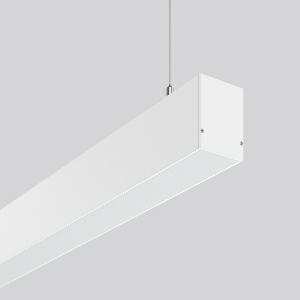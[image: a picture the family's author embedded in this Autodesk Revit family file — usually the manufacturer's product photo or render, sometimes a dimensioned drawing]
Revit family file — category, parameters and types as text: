
# Revit family: less_is_more_50_312320_002_76_c6af
name_source: partatom
category: Lighting Fixtures
units: mm (PartAtom-declared; Revit-internal decimal feet)

## family parameters
Cut with Voids When Loaded = No
Host = Face
Light Source = No
Part Type = Normal
Room Calculation Point = No
Round Connector Dimension = Use Diameter
Shared = No

## types (1)
- LESS IS MORE 50 (1 x LED Modul 830, 6900 lm, 3000)
    Apparent Load = 59 VA
    CIE Flux Codes = 49 80 96 63 100
    Color Rendering = 80
    Color Temperature = 3000
    Default Elevation = 1800 mm
    Description = Series: LESS IS MORE 50
Linear pendant luminaire for aesthetically sophisticated lighting. Housing: extruded aluminium profile, powder-coated. End cap aluminium powder-coated. Canopy made of aluminium, powder-coated. Diffuser made of non-yellowing plastic (PMMA), opal. Direct 65%, indirect 35% light emission. Suitable for pendant. 2-point steel cable suspension freely positionable and infinitely height-adjustable. Special lengths available on request. LED unit with integrated converter interchangeable and removable. Suitable for through-wiring. With sensors or as a safety luminaire on request. 
Colour: traffic white, matt (RAL 9016)
Length: 1687 mm
Width: 57 mm
Height: 75 mm
Suspension length: 2000 mm
Lamp: LED
Socket: without socket
Colour temperature: 3000K
Colour rendering index (CRI): 80
Light source: LED
Socket lamp2: Without base
Colour temperature: 3000K
System power: 59 W
Rated luminous flux: 6900 lm
Luminous efficiency: 117 lm/W
Control gear: Converter, dimmable, DALI
Control gear: Converter, dimmable, DALI
Protection class: I
Type of protection: IP 20
    Height = 75 mm
    Lamp = 1 x LED Modul 830
    Lamp Light Flux = 6900 lm
    Lamp count = 1
    Length = 1687 mm
    Lifetime = 50000 h
    Luminous efficacy = 117 lm/W
    Manufacturer = RZB
    ModVariant = No
    Model = 312320.002.76
    Mounting Place = Ceiling
    Mounting Type = Pendant
    Number of Poles = 1
    OnlyDefault = Yes
    Power Factor = 1
    Product Name = LESS IS MORE 50
    Product group = Pendant LED linear luminaires
    ProductGroupID = 907
    Protection Class = Protection class I
    Protection Degree = IP 20
    RLX_Detail_Level = 1
    RLX_Emergency_Light_Flux = 0 lm
    RLX_Emergency_Type = 0
    RLX_Emergency_Type_DB = No
    RlxData = <blob elided: 31597 chars, md5=cf53522b>
    Socket = socket
    Standby Power = 0 W
    System Light Flux = 6900 lm
    System Power = 59 W
    Type Comments = Product without accessories
    Type Image = 312318.002.jpg
    URL = http://relux.com
    VarID = ---
    Voltage = 230 V
    Voltage Range = 220-240 V
    Weight = 0.00 kg
    Width = 57 mm

## geometry (parser evidence)
native form markers: Blend x4, Sweep x13
no freeform markers — native parametric forms only
